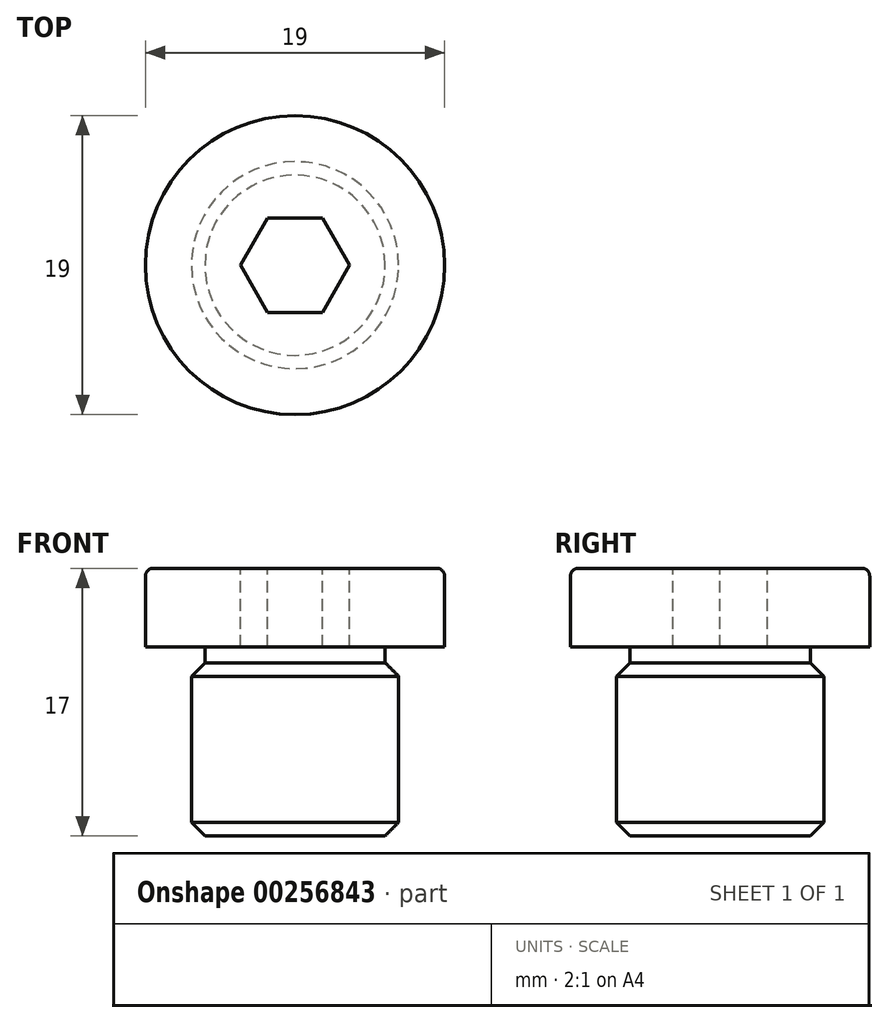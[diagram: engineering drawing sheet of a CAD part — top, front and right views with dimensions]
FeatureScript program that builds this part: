
annotation { "Feature Type Name" : "Feature", "Feature Type Description" : "" }
export const myFeature = defineFeature(function(context is Context, id is Id, definition is map)
    precondition{}
    {
        {
            var Q0;
            Q0=qCreatedBy(makeId("Front.planeOp"),FACE);
            var sketch = newSketch(context, id + "F0", { "sketchPlane" : qUnion([Q0])});
            skLineSegment(sketch, "E0", {"start": v(0, 0) * mm, "end": v(5.72, 0) * mm});
            skLineSegment(sketch, "E1", {"start": v(5.72, 0) * mm, "end": v(6.58, 0.86) * mm});
            skLineSegment(sketch, "E2", {"start": v(6.58, 0.86) * mm, "end": v(6.58, 10.14) * mm});
            skLineSegment(sketch, "E3", {"start": v(6.58, 10.14) * mm, "end": v(5.72, 11) * mm});
            skLineSegment(sketch, "E4", {"start": v(5.72, 11) * mm, "end": v(5.72, 12) * mm});
            skLineSegment(sketch, "E5", {"start": v(5.72, 12) * mm, "end": v(9.5, 12) * mm});
            skLineSegment(sketch, "E6", {"start": v(9.5, 12) * mm, "end": v(9.5, 16.5) * mm});
            skLineSegment(sketch, "E7", {"start": v(9, 17) * mm, "end": v(0, 17) * mm});
            skLineSegment(sketch, "E8", {"start": v(0, 17) * mm, "end": v(0, 0) * mm});
            skPoint(sketch, "E9.visualSharp", {"position": v(9.5, 17) * mm});
            skArc(sketch, "E9.filletArc", {"start": v(9.5, 16.5) * mm, "mid": v(9.35, 16.85) * mm, "end": v(9, 17) * mm});
            skSolve(sketch);
        }
        {
            var Q0;
            Q0 = qSketchRegion(id + "F0", true);
            var Q1;
            Q1=sQuery(id+"F0.wireOp",EDGE,"E8");
            revolve(context, id + "F1", {"entities" : qUnion([Q0]), "axis" : qUnion([Q1]), "revolveType" : RevolveType.FULL});
        }
        {
            var Q0;
            Q0=makeQuery(id+"F1.opRevolve","SWEPT_FACE",FACE,{"disambiguationData":[OSD([sQuery(id+"F0.wireOp",EDGE,"E7")])]});
            var sketch = newSketch(context, id + "F2", { "sketchPlane" : qUnion([Q0])});
            skCircle(sketch, "E10.cCircle", {"center": v(0, 0) * mm, "radius": 3 * mm, "construction": true});
            skLineSegment(sketch, "E10.0", {"start": v(1.73, 3) * mm, "end": v(3.46, 0) * mm});
            skLineSegment(sketch, "E10.1", {"start": v(3.46, 0) * mm, "end": v(1.73, -3) * mm});
            skLineSegment(sketch, "E10.2", {"start": v(1.73, -3) * mm, "end": v(-1.73, -3) * mm});
            skLineSegment(sketch, "E10.3", {"start": v(-1.73, -3) * mm, "end": v(-3.46, 0) * mm});
            skLineSegment(sketch, "E10.4", {"start": v(-3.46, 0) * mm, "end": v(-1.73, 3) * mm});
            skLineSegment(sketch, "E10.5", {"start": v(-1.73, 3) * mm, "end": v(1.73, 3) * mm});
            skPoint(sketch, "E10.0.midPoint", {"position": v(2.6, 1.5) * mm});
            skSolve(sketch);
        }
        {
            var Q0;
            Q0 = qSketchRegion(id + "F2", true);
            extrude(context, id + "F3", {"entities" : qUnion([Q0]), "operationType" : NewBodyOperationType.REMOVE, "oppositeDirection" : true, "depth" : 5 * mm});
        }
    });
